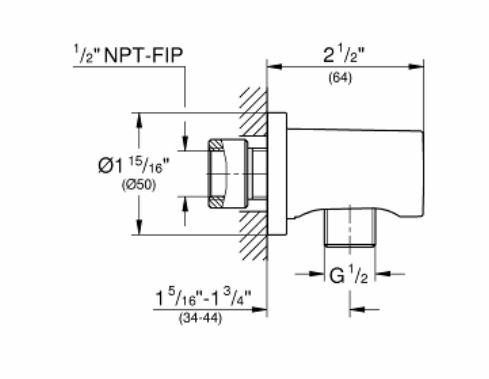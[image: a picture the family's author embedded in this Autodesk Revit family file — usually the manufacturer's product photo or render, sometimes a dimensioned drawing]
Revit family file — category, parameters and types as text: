
# Revit family: Commercial_Shower_System-GROHE-Timeless-29431_Series
name_source: partatom
category: Plumbing Fixtures
units: mm (PartAtom-declared; Revit-internal decimal feet)

## family parameters
Cut with Voids When Loaded = No
Host = Face
OmniClass Number = 23.45.05.14.17
OmniClass Title = Showers
Part Type = Normal
Room Calculation Point = No
Round Connector Dimension = Use Diameter
Shared = Yes

## types (4) — shared parameters
26 547- Rainshower™ SmartActive 24” Shower Set, 3 sprays, 1.75gpm = Yes
26 635- Rainshower™ Wall Union = Yes
26 789- Rainshower™ SmartActive 6 ½” shower head, 3 sprays, 1.75gpm = Yes
27 412- Relexa® 6 ¼” shower arm = Yes
29 423- Timeless Pressure Balance Valve Trim with 2-Way Diverter = Yes
35 117- GrohSafe™ 3.0 Pressure Balance Rough Valve with Integrated Diverter = Yes
ASME A112.18.1/CSA B125.1/ASSE 1016 = Yes
ASSE 1016 = Yes
Assembly Code = D2010710
CEC Compliant = Yes
CW Connection = Yes
CWFU = 3
CalGreen Compliant = Yes
Cold Water Connection Diameter = 1/2"
Connection Diameter = 1/2"
Default Elevation = 0"
Description = TIMELESS- Pressure Balance Shower Set
Double check valves = Included
EPA WaterSense® Certified = Yes
Flow Rate = Max. 1.75gpm (6.6L/min)
HW Connection = Yes
HWFU = 3
Height- Diverter = 48"
Height- Showerhead = 78"
Hot Water Connection Diameter = 1/2"
IAPMO Compliance = Massachusetts Plumbing Board Approved, Energy Policy Act of 1992, CSA B125.16
Installation Type = Wall Mounted
Manufacturer = GROHE
Price = Prices may vary. Please consult Manufacturer Representative for most up-to-date price list.
Tempered Water Connection = Yes
URL = https://www.grohe.us
Vent Connection = No
WFU = 4
Waste Connection = No

## per-type parameters (varying)
| type | Finish | Material |
| 29431000 | Metal-Grohe-000-StarLight Chrome | Metal-Grohe-000-StarLight Chrome |
| 29431A00 | Metal-Grohe-A00-Hard Graphite | Metal-Grohe-A00-Hard Graphite |
| 29431EN0 | Metal-Grohe-EN0-Brushed Nickel Infinity Finish | Metal-Grohe-EN0-Brushed Nickel Infinity Finish |
| 29431GN0 | Metal-Grohe-GN0-Brushed Cool Sunrise | Metal-Grohe-GN0-Brushed Cool Sunrise |

note: column(s) folded — value = type name in every type: Model

## geometry (parser evidence)
native form markers: Sweep x19
no freeform markers — native parametric forms only
